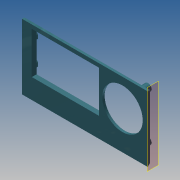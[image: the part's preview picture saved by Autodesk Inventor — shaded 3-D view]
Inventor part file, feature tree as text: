
AUTODESK INVENTOR PART (.ipt)
format: ipt  version: 2013 (Build 170138000, 138)  size: 174,592 bytes
history: native  units: in
note: dims shown in document units (in); Inventor stores cm internally (conversion verified against a paired STEP export)
features: extrude x8, sketch x8, reference x8, plane x2, chamfer x1
ambient origin geometry x8: Origin, YZ Plane, XZ Plane, XY Plane, X Axis, Y Axis, Z Axis, Center Point
bodies: Solid1 (feature_tree)
feature tree (27):
  plane  "Work Plane1"
  extrude  "Extrusion1"  Depth=0.0098in
  extrude  "Extrusion2"  Depth=0.0394in
  chamfer  "Chamfer1"  Distance=105.7in
  extrude  "Extrusion3"  Depth=105.7in TaperAngle=0.0deg
  sketch  "Sketch4"  dims[d12=0.2362in d14=105.7in d15=0.0in]
  plane  "Work Plane2"
  extrude  "Extrusion4"  Depth=105.7in TaperAngle=0.0deg
  extrude  "Extrusion5"  Depth=0.0197in TaperAngle=0.0deg
  extrude  "Extrusion6"  Depth=0.5in TaperAngle=0.0deg
  extrude  "Extrusion7"  Depth=0.0315in
  extrude  "Extrusion8"  [1 undecoded]
  sketch  "Sketch1"  dims[d0=0.0098in d1=0.0098in]
  reference  "Reference1"
  reference  "Reference2"
  sketch  "Sketch2"  dims[d2=4.1614in d3=0.0in d4=0.0394in d5=105.7in d6=0.0in]
  reference  "Reference3"
  reference  "Reference4"
  sketch  "Sketch3"  dims[d7=0.0787in d8=0.125in d9=45.0deg d10=105.7in d11=0.0in]
  reference  "Reference5"
  sketch  "Sketch5"  dims[d16=0.0in d17=0.0in d18=0.0197in d19=0.0in]
  sketch  "Sketch6"  dims[d20=0.1181in d22=0.5in d23=0.0in]
  sketch  "Sketch7"  dims[d24=0.0315in d25=0.0315in]
  reference  "Reference6"
  reference  "Reference7"
  reference  "Reference8"
  sketch  "Sketch8"  dims[d26=0.5in d27=0.0in]
note: 1 required parameter value undecoded (feature->parameter linkage not recoverable at this tier; creation-order binding heuristic only, values carry confidence <= 0.55)
